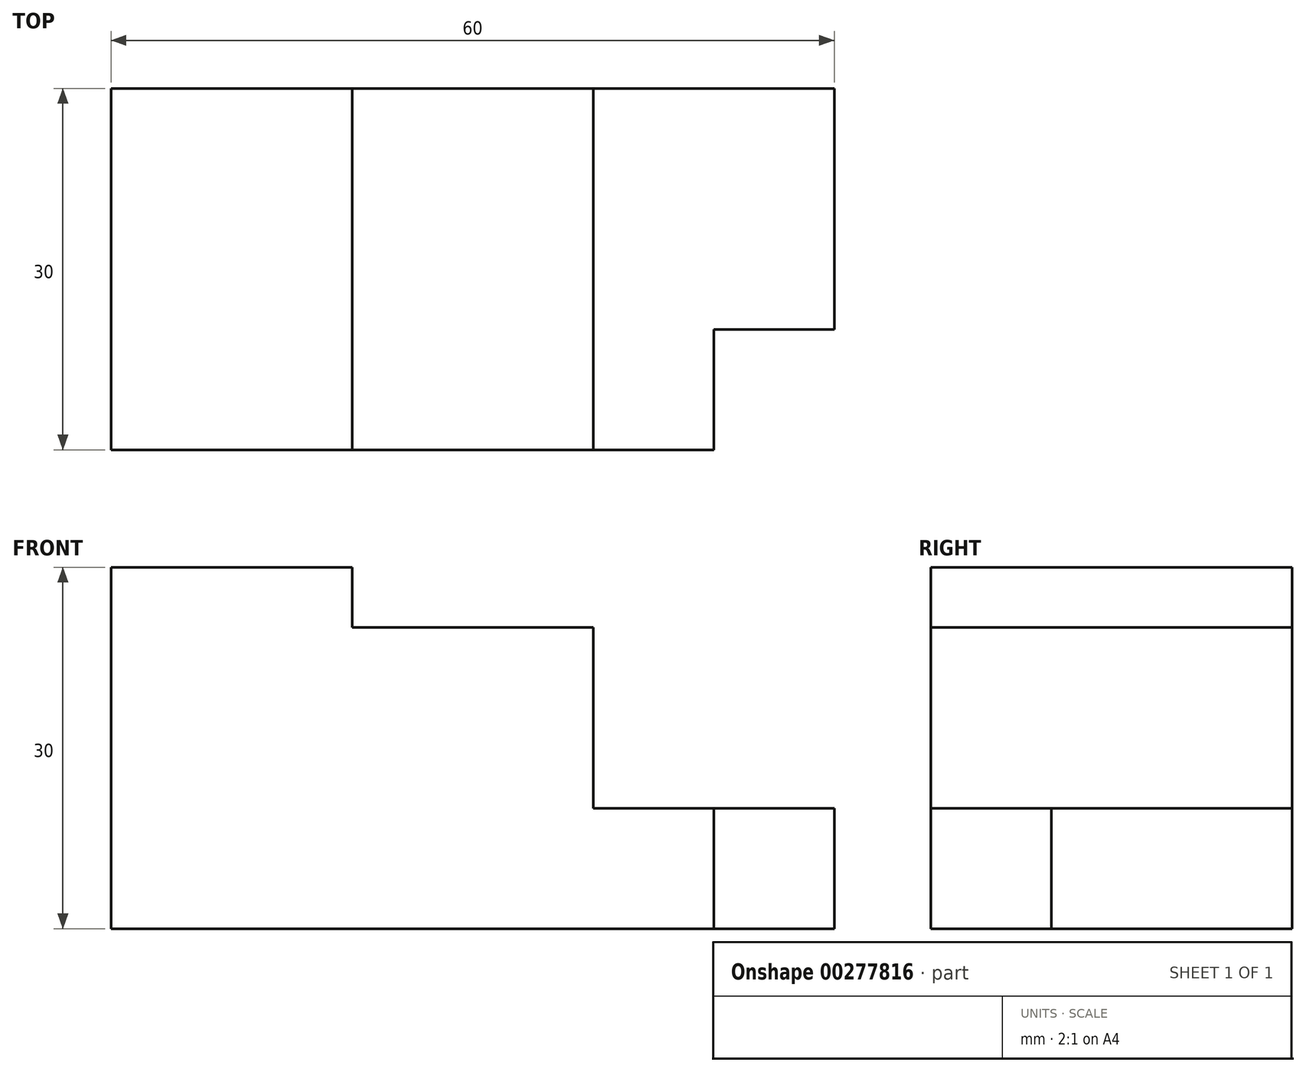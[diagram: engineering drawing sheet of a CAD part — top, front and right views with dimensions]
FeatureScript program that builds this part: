
annotation { "Feature Type Name" : "Feature", "Feature Type Description" : "" }
export const myFeature = defineFeature(function(context is Context, id is Id, definition is map)
    precondition{}
    {
        {
            var Q0;
            Q0=qCreatedBy(makeId("Top.planeOp"),FACE);
            var sketch = newSketch(context, id + "F0", { "sketchPlane" : qUnion([Q0])});
            skLineSegment(sketch, "E0.bottom", {"start": v(0, 0) * mm, "end": v(60, 0) * mm});
            skLineSegment(sketch, "E0.top", {"start": v(0, 30) * mm, "end": v(60, 30) * mm});
            skLineSegment(sketch, "E0.left", {"start": v(0, 0) * mm, "end": v(0, 30) * mm});
            skLineSegment(sketch, "E0.right", {"start": v(60, 0) * mm, "end": v(60, 30) * mm});
            skSolve(sketch);
        }
        {
            var Q0;
            Q0=makeQuery(id+"F0.imprint","IMPRINT",FACE,{"disambiguationData":[TD([[makeQuery(id+"F0.imprint","IMPRINT",EDGE,{"derivedFrom":sQuery(id+"F0.wireOp",EDGE,"E0.bottom")}),1.0]])]});
            extrude(context, id + "F1", {"entities" : qUnion([Q0]), "depth" : 30 * mm});
        }
        {
            var Q0;
            Q0=makeQuery(id+"F1.opExtrude","CAP_FACE",FACE,{"disambiguationData":[OSD([sQuery(id+"F0.wireOp",EDGE,"E0.bottom"),sQuery(id+"F0.wireOp",EDGE,"E0.top"),sQuery(id+"F0.wireOp",EDGE,"E0.left"),sQuery(id+"F0.wireOp",EDGE,"E0.right")])],"isStart":false});
            var sketch = newSketch(context, id + "F2", { "sketchPlane" : qUnion([Q0])});
            skLineSegment(sketch, "E1", {"start": v(20, 0) * mm, "end": v(20, 30) * mm});
            skLineSegment(sketch, "E2", {"start": v(40, 30) * mm, "end": v(40, 0) * mm});
            skLineSegment(sketch, "E3", {"start": v(50, 0) * mm, "end": v(50, 10) * mm});
            skLineSegment(sketch, "E4", {"start": v(50, 10) * mm, "end": v(60, 10) * mm});
            skSolve(sketch);
        }
        {
            var Q0;
            {var subQ0=sQuery(id+"F2.wireOp",EDGE,"E1");Q0=makeQuery(id+"F2.imprint","IMPRINT",FACE,{"disambiguationData":[TD([[makeQuery(id+"F2.imprint","IMPRINT",EDGE,{"derivedFrom":subQ0}),-1.0]])]});}
            extrude(context, id + "F3", {"entities" : qUnion([Q0]), "operationType" : NewBodyOperationType.REMOVE, "oppositeDirection" : true, "depth" : 5 * mm});
        }
        {
            var Q0;
            {var subQ0=sQuery(id+"F0.wireOp",EDGE,"E0.bottom");var subQ1=sQuery(id+"F0.wireOp",EDGE,"E0.top");var subQ2=sQuery(id+"F0.wireOp",EDGE,"E0.right");Q0=makeQuery(id+"F3.boolean.opBoolean","SPLIT",FACE,{"disambiguationData":[TD([makeQuery(id+"F1.opExtrude","SWEPT_FACE",FACE,{"disambiguationData":[OSD([subQ2])]})])],"derivedFrom":makeQuery(id+"F1.opExtrude","CAP_FACE",FACE,{"disambiguationData":[OSD([subQ0,subQ1,sQuery(id+"F0.wireOp",EDGE,"E0.left"),subQ2])],"isStart":false})});}
            extrude(context, id + "F4", {"entities" : qUnion([Q0]), "operationType" : NewBodyOperationType.REMOVE, "oppositeDirection" : true, "depth" : 20 * mm});
        }
        {
            var Q0;
            {var subQ0=sQuery(id+"F2.wireOp",EDGE,"E3");Q0=makeQuery(id+"F2.imprint","IMPRINT",FACE,{"disambiguationData":[TD([[makeQuery(id+"F2.imprint","IMPRINT",EDGE,{"derivedFrom":subQ0}),-1.0]])]});}
            extrude(context, id + "F5", {"entities" : qUnion([Q0]), "operationType" : NewBodyOperationType.REMOVE, "endBound" : BoundingType.THROUGH_ALL, "oppositeDirection" : true, "depth" : 25 * mm});
        }
    });
